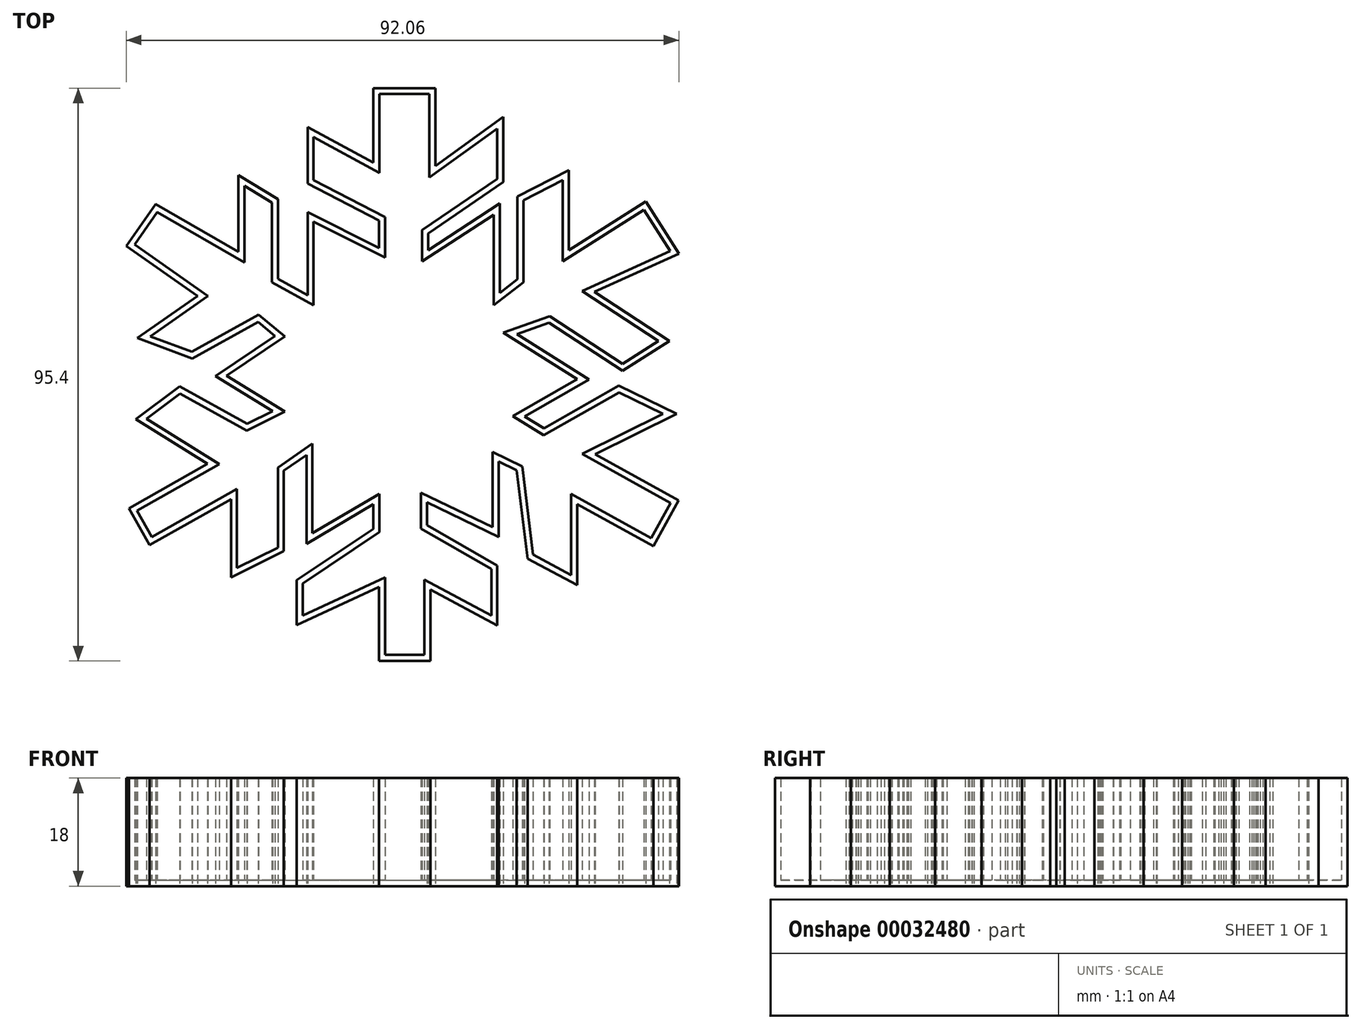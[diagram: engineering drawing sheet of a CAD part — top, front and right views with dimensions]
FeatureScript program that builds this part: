
annotation { "Feature Type Name" : "Feature", "Feature Type Description" : "" }
export const myFeature = defineFeature(function(context is Context, id is Id, definition is map)
    precondition{}
    {
        {
            var Q0;
            Q0=qCreatedBy(makeId("Top.planeOp"),FACE);
            var sketch = newSketch(context, id + "F0", { "sketchPlane" : qUnion([Q0])});
            skLineSegment(sketch, "E0", {"start": v(-42.28, 11.68) * mm, "end": v(-46.05, 6.31) * mm});
            skLineSegment(sketch, "E1", {"start": v(-46.05, 6.31) * mm, "end": v(-33.85, -2.28) * mm});
            skLineSegment(sketch, "E2", {"start": v(-33.85, -2.28) * mm, "end": v(-43.47, -9) * mm});
            skLineSegment(sketch, "E3", {"start": v(-43.47, -9) * mm, "end": v(-36.52, -11.57) * mm});
            skLineSegment(sketch, "E4", {"start": v(-36.52, -11.57) * mm, "end": v(-25.39, -5.41) * mm});
            skLineSegment(sketch, "E5", {"start": v(-25.39, -5.41) * mm, "end": v(-21.01, -9) * mm});
            skLineSegment(sketch, "E6", {"start": v(-21.01, -9) * mm, "end": v(-30.75, -15.55) * mm});
            skLineSegment(sketch, "E7", {"start": v(-30.75, -15.55) * mm, "end": v(-21.01, -21.51) * mm});
            skLineSegment(sketch, "E8", {"start": v(-21.01, -21.51) * mm, "end": v(-27.37, -24.7) * mm});
            skLineSegment(sketch, "E9", {"start": v(-27.37, -24.7) * mm, "end": v(-38.5, -18.53) * mm});
            skLineSegment(sketch, "E10", {"start": v(-38.5, -18.53) * mm, "end": v(-44.07, -22.7) * mm});
            skLineSegment(sketch, "E11", {"start": v(-44.07, -22.7) * mm, "end": v(-31.94, -30.25) * mm});
            skLineSegment(sketch, "E12", {"start": v(-31.94, -30.25) * mm, "end": v(-45.66, -38) * mm});
            skLineSegment(sketch, "E13", {"start": v(-45.66, -38) * mm, "end": v(-43.17, -42.4) * mm});
            skLineSegment(sketch, "E14", {"start": v(-43.17, -42.4) * mm, "end": v(-29, -34.4) * mm});
            skLineSegment(sketch, "E15", {"start": v(-29, -34.4) * mm, "end": v(-29, -47.54) * mm});
            skLineSegment(sketch, "E16", {"start": v(-29, -47.54) * mm, "end": v(-22.2, -44.17) * mm});
            skLineSegment(sketch, "E17", {"start": v(-22.2, -44.17) * mm, "end": v(-22.2, -30.85) * mm});
            skLineSegment(sketch, "E18", {"start": v(-22.2, -30.85) * mm, "end": v(-16.44, -26.88) * mm});
            skLineSegment(sketch, "E19", {"start": v(-16.44, -26.88) * mm, "end": v(-16.44, -41.78) * mm});
            skLineSegment(sketch, "E20", {"start": v(-16.44, -41.78) * mm, "end": v(-5.31, -35.22) * mm});
            skLineSegment(sketch, "E21", {"start": v(-5.31, -35.22) * mm, "end": v(-5.31, -41.58) * mm});
            skLineSegment(sketch, "E22", {"start": v(-5.31, -41.58) * mm, "end": v(-18.03, -50.13) * mm});
            skLineSegment(sketch, "E23", {"start": v(-18.03, -50.13) * mm, "end": v(-18.03, -55.5) * mm});
            skLineSegment(sketch, "E24", {"start": v(-18.03, -55.5) * mm, "end": v(-4.32, -49.13) * mm});
            skLineSegment(sketch, "E25", {"start": v(-4.32, -49.13) * mm, "end": v(-4.32, -62.05) * mm});
            skLineSegment(sketch, "E26", {"start": v(-4.32, -62.05) * mm, "end": v(2.24, -62.05) * mm});
            skLineSegment(sketch, "E27", {"start": v(2.24, -62.05) * mm, "end": v(2.24, -49.53) * mm});
            skLineSegment(sketch, "E28", {"start": v(2.24, -49.53) * mm, "end": v(13.37, -55.5) * mm});
            skLineSegment(sketch, "E29", {"start": v(13.37, -55.5) * mm, "end": v(13.37, -47.74) * mm});
            skLineSegment(sketch, "E30", {"start": v(13.37, -47.74) * mm, "end": v(1.64, -40.99) * mm});
            skLineSegment(sketch, "E31", {"start": v(1.64, -40.99) * mm, "end": v(1.64, -35.02) * mm});
            skLineSegment(sketch, "E32", {"start": v(1.64, -35.02) * mm, "end": v(13.56, -40.79) * mm});
            skLineSegment(sketch, "E33", {"start": v(13.56, -40.79) * mm, "end": v(13.56, -28.27) * mm});
            skLineSegment(sketch, "E34", {"start": v(13.56, -28.27) * mm, "end": v(18.53, -30.65) * mm});
            skLineSegment(sketch, "E35", {"start": v(18.53, -30.65) * mm, "end": v(20.32, -45.36) * mm});
            skLineSegment(sketch, "E36", {"start": v(20.32, -45.36) * mm, "end": v(26.68, -48.74) * mm});
            skLineSegment(sketch, "E37", {"start": v(26.68, -48.74) * mm, "end": v(26.68, -35.22) * mm});
            skLineSegment(sketch, "E38", {"start": v(26.68, -35.22) * mm, "end": v(40, -42.58) * mm});
            skLineSegment(sketch, "E39", {"start": v(40, -42.58) * mm, "end": v(43.22, -36.73) * mm});
            skLineSegment(sketch, "E40", {"start": v(43.22, -36.73) * mm, "end": v(28.47, -28.58) * mm});
            skLineSegment(sketch, "E41", {"start": v(28.47, -28.58) * mm, "end": v(41.98, -21.9) * mm});
            skLineSegment(sketch, "E42", {"start": v(41.98, -21.9) * mm, "end": v(34.63, -18.33) * mm});
            skLineSegment(sketch, "E43", {"start": v(34.63, -18.33) * mm, "end": v(22.1, -25.49) * mm});
            skLineSegment(sketch, "E44", {"start": v(22.1, -25.49) * mm, "end": v(16.94, -22.3) * mm});
            skLineSegment(sketch, "E45", {"start": v(16.94, -22.3) * mm, "end": v(27.67, -16.14) * mm});
            skLineSegment(sketch, "E46", {"start": v(27.67, -16.14) * mm, "end": v(15.35, -8.4) * mm});
            skLineSegment(sketch, "E47", {"start": v(-42.28, 11.68) * mm, "end": v(-27.77, 3.33) * mm});
            skLineSegment(sketch, "E48", {"start": v(-27.77, 3.33) * mm, "end": v(-27.77, 16.05) * mm});
            skLineSegment(sketch, "E49", {"start": v(-27.77, 16.05) * mm, "end": v(-23.2, 13.27) * mm});
            skLineSegment(sketch, "E50", {"start": v(-23.2, 13.27) * mm, "end": v(-23.2, 0) * mm});
            skLineSegment(sketch, "E51", {"start": v(-23.2, 0) * mm, "end": v(-16.25, -3.82) * mm});
            skLineSegment(sketch, "E52", {"start": v(-16.25, -3.82) * mm, "end": v(-16.25, 10.09) * mm});
            skLineSegment(sketch, "E53", {"start": v(-16.25, 10.09) * mm, "end": v(-4.32, 4.13) * mm});
            skLineSegment(sketch, "E54", {"start": v(-4.32, 4.13) * mm, "end": v(-4.32, 10.88) * mm});
            skLineSegment(sketch, "E55", {"start": v(-4.32, 10.88) * mm, "end": v(-16.25, 17.04) * mm});
            skLineSegment(sketch, "E56", {"start": v(-16.25, 17.04) * mm, "end": v(-16.25, 24.2) * mm});
            skLineSegment(sketch, "E57", {"start": v(-16.25, 24.2) * mm, "end": v(-5.31, 18.24) * mm});
            skLineSegment(sketch, "E58", {"start": v(-5.31, 18.24) * mm, "end": v(-5.31, 31.35) * mm});
            skLineSegment(sketch, "E59", {"start": v(-5.31, 31.35) * mm, "end": v(3.03, 31.35) * mm});
            skLineSegment(sketch, "E60", {"start": v(3.03, 31.35) * mm, "end": v(3.03, 17.44) * mm});
            skLineSegment(sketch, "E61", {"start": v(3.03, 17.44) * mm, "end": v(14.36, 25.59) * mm});
            skLineSegment(sketch, "E62", {"start": v(14.36, 25.59) * mm, "end": v(14.36, 17.24) * mm});
            skLineSegment(sketch, "E63", {"start": v(14.36, 17.24) * mm, "end": v(1.84, 8.7) * mm});
            skLineSegment(sketch, "E64", {"start": v(1.84, 8.7) * mm, "end": v(1.84, 3.53) * mm});
            skLineSegment(sketch, "E65", {"start": v(1.84, 3.53) * mm, "end": v(13.76, 11.28) * mm});
            skLineSegment(sketch, "E66", {"start": v(13.76, 11.28) * mm, "end": v(13.76, -3.82) * mm});
            skLineSegment(sketch, "E67", {"start": v(13.76, -3.82) * mm, "end": v(18.73, 0) * mm});
            skLineSegment(sketch, "E68", {"start": v(18.73, 0) * mm, "end": v(18.73, 13.66) * mm});
            skLineSegment(sketch, "E69", {"start": v(18.73, 13.66) * mm, "end": v(25.29, 17.04) * mm});
            skLineSegment(sketch, "E70", {"start": v(25.29, 17.04) * mm, "end": v(25.29, 3.53) * mm});
            skLineSegment(sketch, "E71", {"start": v(25.29, 3.53) * mm, "end": v(38.8, 12.07) * mm});
            skLineSegment(sketch, "E72", {"start": v(38.8, 12.07) * mm, "end": v(43.15, 5.2) * mm});
            skLineSegment(sketch, "E73", {"start": v(43.15, 5.2) * mm, "end": v(28.47, -1.44) * mm});
            skLineSegment(sketch, "E74", {"start": v(28.47, -1.44) * mm, "end": v(41.19, -9.79) * mm});
            skLineSegment(sketch, "E75", {"start": v(41.19, -9.79) * mm, "end": v(35.23, -13.56) * mm});
            skLineSegment(sketch, "E76", {"start": v(35.23, -13.56) * mm, "end": v(23.1, -5.61) * mm});
            skLineSegment(sketch, "E77", {"start": v(23.1, -5.61) * mm, "end": v(15.35, -8.4) * mm});
            skSolve(sketch);
        }
        {
            var Q0;
            Q0=makeQuery(id+"F0.imprint","IMPRINT",FACE,{"disambiguationData":[TD([[makeQuery(id+"F0.imprint","IMPRINT",EDGE,{"derivedFrom":sQuery(id+"F0.wireOp",EDGE,"E0")}),1.0]])]});
            extrude(context, id + "F1", {"entities" : qUnion([Q0]), "depth" : 17 * mm});
        }
        {
            var Q0;
            Q0=makeQuery(id+"F1.opExtrude","CAP_FACE",FACE,{"disambiguationData":[OSD([sQuery(id+"F0.wireOp",EDGE,"E0"),sQuery(id+"F0.wireOp",EDGE,"E1"),sQuery(id+"F0.wireOp",EDGE,"E2"),sQuery(id+"F0.wireOp",EDGE,"E3"),sQuery(id+"F0.wireOp",EDGE,"E4"),sQuery(id+"F0.wireOp",EDGE,"E5"),sQuery(id+"F0.wireOp",EDGE,"E6"),sQuery(id+"F0.wireOp",EDGE,"E7"),sQuery(id+"F0.wireOp",EDGE,"E8"),sQuery(id+"F0.wireOp",EDGE,"E9"),sQuery(id+"F0.wireOp",EDGE,"E10"),sQuery(id+"F0.wireOp",EDGE,"E11"),sQuery(id+"F0.wireOp",EDGE,"E12"),sQuery(id+"F0.wireOp",EDGE,"E13"),sQuery(id+"F0.wireOp",EDGE,"E14"),sQuery(id+"F0.wireOp",EDGE,"E15"),sQuery(id+"F0.wireOp",EDGE,"E16"),sQuery(id+"F0.wireOp",EDGE,"E17"),sQuery(id+"F0.wireOp",EDGE,"E18"),sQuery(id+"F0.wireOp",EDGE,"E19"),sQuery(id+"F0.wireOp",EDGE,"E20"),sQuery(id+"F0.wireOp",EDGE,"E21"),sQuery(id+"F0.wireOp",EDGE,"E22"),sQuery(id+"F0.wireOp",EDGE,"E23"),sQuery(id+"F0.wireOp",EDGE,"E24"),sQuery(id+"F0.wireOp",EDGE,"E25"),sQuery(id+"F0.wireOp",EDGE,"E26"),sQuery(id+"F0.wireOp",EDGE,"E27"),sQuery(id+"F0.wireOp",EDGE,"E28"),sQuery(id+"F0.wireOp",EDGE,"E29"),sQuery(id+"F0.wireOp",EDGE,"E30"),sQuery(id+"F0.wireOp",EDGE,"E31"),sQuery(id+"F0.wireOp",EDGE,"E32"),sQuery(id+"F0.wireOp",EDGE,"E33"),sQuery(id+"F0.wireOp",EDGE,"E34"),sQuery(id+"F0.wireOp",EDGE,"E35"),sQuery(id+"F0.wireOp",EDGE,"E36"),sQuery(id+"F0.wireOp",EDGE,"E37"),sQuery(id+"F0.wireOp",EDGE,"E38"),sQuery(id+"F0.wireOp",EDGE,"E39"),sQuery(id+"F0.wireOp",EDGE,"E40"),sQuery(id+"F0.wireOp",EDGE,"E41"),sQuery(id+"F0.wireOp",EDGE,"E42"),sQuery(id+"F0.wireOp",EDGE,"E43"),sQuery(id+"F0.wireOp",EDGE,"E44"),sQuery(id+"F0.wireOp",EDGE,"E45"),sQuery(id+"F0.wireOp",EDGE,"E46"),sQuery(id+"F0.wireOp",EDGE,"E47"),sQuery(id+"F0.wireOp",EDGE,"E48"),sQuery(id+"F0.wireOp",EDGE,"E49"),sQuery(id+"F0.wireOp",EDGE,"E50"),sQuery(id+"F0.wireOp",EDGE,"E51"),sQuery(id+"F0.wireOp",EDGE,"E52"),sQuery(id+"F0.wireOp",EDGE,"E53"),sQuery(id+"F0.wireOp",EDGE,"E54"),sQuery(id+"F0.wireOp",EDGE,"E55"),sQuery(id+"F0.wireOp",EDGE,"E56"),sQuery(id+"F0.wireOp",EDGE,"E57"),sQuery(id+"F0.wireOp",EDGE,"E58"),sQuery(id+"F0.wireOp",EDGE,"E59"),sQuery(id+"F0.wireOp",EDGE,"E60"),sQuery(id+"F0.wireOp",EDGE,"E61"),sQuery(id+"F0.wireOp",EDGE,"E62"),sQuery(id+"F0.wireOp",EDGE,"E63"),sQuery(id+"F0.wireOp",EDGE,"E64"),sQuery(id+"F0.wireOp",EDGE,"E65"),sQuery(id+"F0.wireOp",EDGE,"E66"),sQuery(id+"F0.wireOp",EDGE,"E67"),sQuery(id+"F0.wireOp",EDGE,"E68"),sQuery(id+"F0.wireOp",EDGE,"E69"),sQuery(id+"F0.wireOp",EDGE,"E70"),sQuery(id+"F0.wireOp",EDGE,"E71"),sQuery(id+"F0.wireOp",EDGE,"E72"),sQuery(id+"F0.wireOp",EDGE,"E73"),sQuery(id+"F0.wireOp",EDGE,"E74"),sQuery(id+"F0.wireOp",EDGE,"E75"),sQuery(id+"F0.wireOp",EDGE,"E76"),sQuery(id+"F0.wireOp",EDGE,"E77")])],"isStart":false});
            shell(context, id + "F2", {"entities" : qUnion([Q0]), "thickness" : 1 * mm, "oppositeDirection" : true});
        }
    });
